# Revit family: BRG-GRF-DCH-BRAZO DE DUCHA CUADRADO 38 CM CROMO
name_source: partatom
category: Aparatos sanitarios
units: mm (PartAtom-declared; Revit-internal decimal feet)

## family parameters
Compartido = Sí
Corte con vacíos al cargar = No
Cota de conector redondo = Diámetro de uso
Número OmniClass = 23.45.00.00
Punto de cálculo de habitación = Sí
Se basa en plano de trabajo = No
Siempre vertical = Sí
Tipo de pieza = Normal
Título OmniClass = Sanitary, Laundry, and Cleaning Equipment

## types (1)
- BRAZO DE DUCHA CUADRADO 38 CM CROMO
    Conexión AC = Sí
    Conexión AF = Sí
    Conexión de residuos = Sí
    Conexión de ventilación = Sí
    Elevación por defecto = 0 m
    Fabricante = BRIGGS Ecuador
    Imagen de tipo = <Ninguno>
    Modelo = _Edesa_ INODORO ANDES C/A BLANCO
    URL = https://www.briggs.com.ec
    _ALT_Altura de ducha = 0.34 m
    _EDESA_ Alto en cm = 6
    _EDESA_ Ancho en cm = 6
    _EDESA_ Categoría = Productos > Grifería > Ducha
    _EDESA_ Certificación = Cumple con norma NTE - INEN 3123 basada en la norma ASME 112.18.1 - 2012.
    _EDESA_ Color = cromo
    _EDESA_ Conexión hidráulica = Entrada de agua: tubería ø 1/2"
    _EDESA_ Descripción = Brazo de ducha
    _EDESA_ Garantía = De por vida para el cuerpo principal y acabado en cromo (306)
    _EDESA_ Manual de Instalación = https://www.briggs.com.ec
    _EDESA_ Marca = BRIGGS
    _EDESA_ Materiales = Latón
    _EDESA_ Nombre = BRAZO DE DUCHA CUADRADO 38 CM
    _EDESA_ Peso en kg = 0.4 kg
    _EDESA_ Productos necesarios para instalación = Regadera
    _EDESA_ Profundidad en cm = 38
    _EDESA_ Sku/código = SG0086483061CW
    _EDESA_ Tipo de instalación = A la pared
